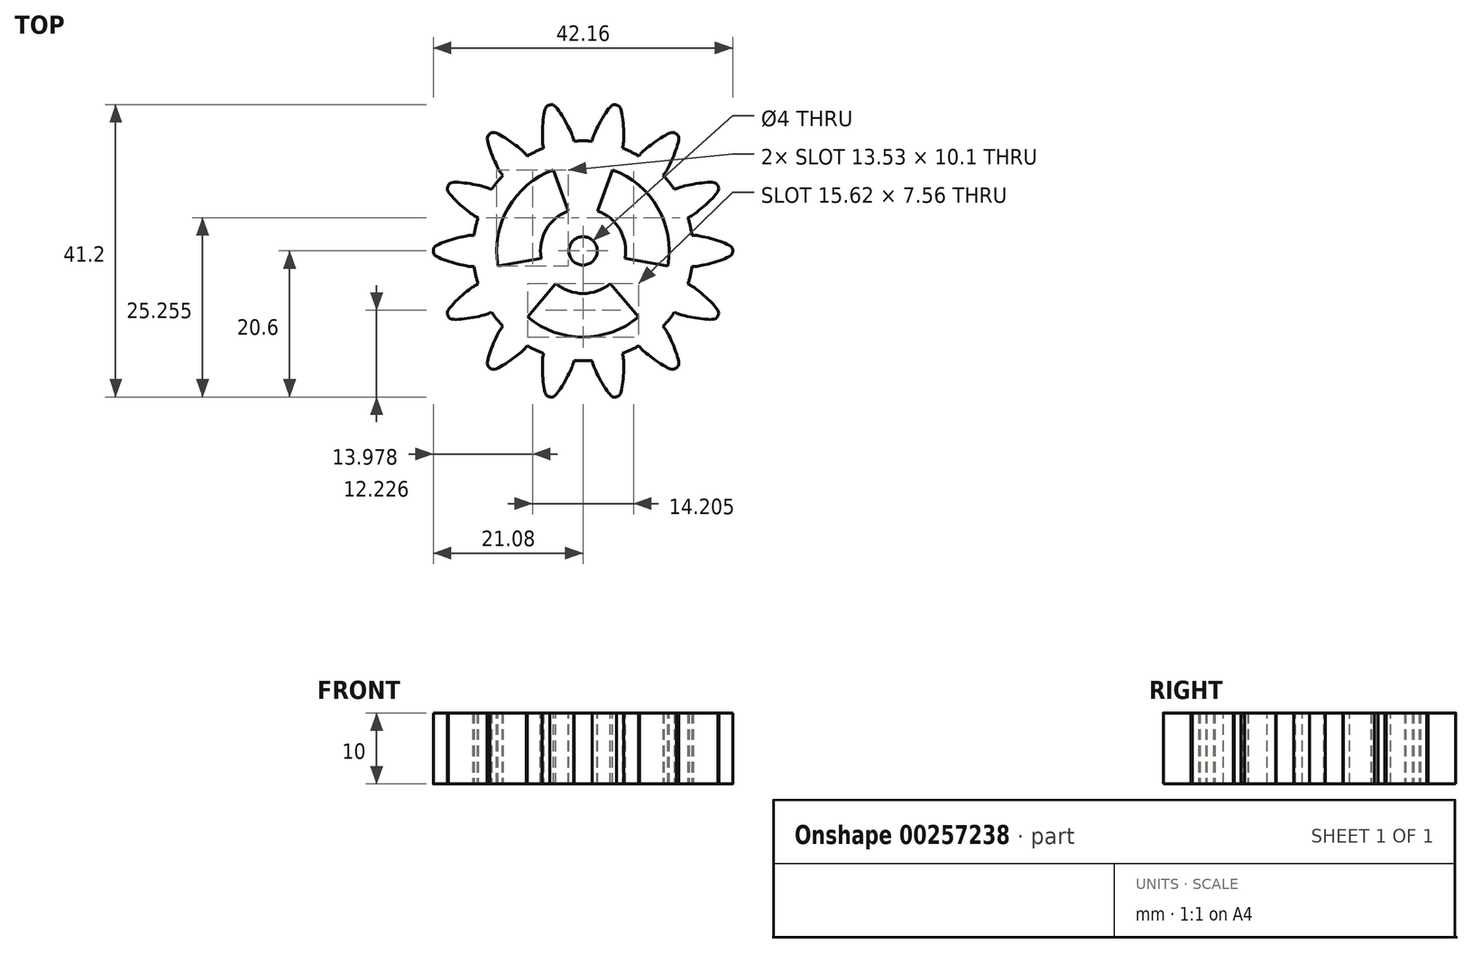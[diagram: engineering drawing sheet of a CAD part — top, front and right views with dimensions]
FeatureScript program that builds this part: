
annotation { "Feature Type Name" : "Feature", "Feature Type Description" : "" }
export const myFeature = defineFeature(function(context is Context, id is Id, definition is map)
    precondition{}
    {
        {
            var Q0;
            Q0=qCreatedBy(makeId("Top.planeOp"),FACE);
            var sketch = newSketch(context, id + "F0", { "sketchPlane" : qUnion([Q0])});
            skLineSegment(sketch, "E0.bottom", {"start": v(-13.86, -2.2) * mm, "end": v(-15.52, -2.2) * mm});
            skLineSegment(sketch, "E0.top", {"start": v(-13.86, 2.2) * mm, "end": v(-15.52, 2.2) * mm});
            skLineSegment(sketch, "E0.left", {"start": v(-13.86, -2.2) * mm, "end": v(-13.86, 2.2) * mm});
            skLineSegment(sketch, "E0.right", {"start": v(-15.52, -2.2) * mm, "end": v(-15.52, 2.2) * mm});
            skPoint(sketch, "E0.middle", {"position": v(-14.69, 0) * mm});
            skFitSpline(sketch, "E1", {"points": [v(-15.52, 2.2) * mm, v(-16.5, 2.1) * mm, v(-20.82, 0.63) * mm, v(-21.08, 0) * mm], "startDerivative": vector(-2.71, 0.04) * mm, "endDerivative": vector(0.07, -2.94) * mm});
            skLineSegment(sketch, "E2", {"start": v(-21.08, 0) * mm, "end": v(-15.52, 0) * mm});
            skFitSpline(sketch, "E3.MirrorCS", {"points": [v(-15.52, -2.2) * mm, v(-16.5, -2.1) * mm, v(-20.82, -0.63) * mm, v(-21.08, 0) * mm], "startDerivative": vector(-2.71, -0.04) * mm, "endDerivative": vector(0.07, 2.94) * mm});
            skCircle(sketch, "E4", {"center": v(0, 0) * mm, "radius": 5.34 * mm});
            skSolve(sketch);
        }
        {
            var Q0;
            Q0=makeQuery(id+"F0.imprint","IMPRINT",FACE,{"disambiguationData":[TD([[makeQuery(id+"F0.imprint","IMPRINT",EDGE,{"derivedFrom":sQuery(id+"F0.wireOp",EDGE,"E4")}),1.0]])]});
            extrude(context, id + "F1", {"entities" : qUnion([Q0]), "depth" : 10 * mm});
        }
        {
            var Q0;
            {var subQ0=sQuery(id+"F0.wireOp",EDGE,"E1");Q0=makeQuery(id+"F0.imprint","IMPRINT",FACE,{"disambiguationData":[TD([[makeQuery(id+"F0.imprint","IMPRINT",EDGE,{"derivedFrom":subQ0}),1.0]])]});}
            var Q1;
            {var subQ1=sQuery(id+"F0.wireOp",EDGE,"E0.bottom");Q1=makeQuery(id+"F0.imprint","IMPRINT",FACE,{"disambiguationData":[TD([[makeQuery(id+"F0.imprint","IMPRINT",EDGE,{"derivedFrom":subQ1}),-1.0]])]});}
            var Q2;
            {var subQ2=sQuery(id+"F0.wireOp",EDGE,"E2");Q2=makeQuery(id+"F0.imprint","IMPRINT",FACE,{"disambiguationData":[TD([[makeQuery(id+"F0.imprint","IMPRINT",EDGE,{"derivedFrom":subQ2}),-1.0]])]});}
            extrude(context, id + "F2", {"entities" : qUnion([Q0, Q1, Q2]), "depth" : 10 * mm});
        }
        {
            var Q0;
            Q0=makeQuery(id+"F2.opExtrude","SWEPT_BODY",BODY,{"disambiguationData":[OSD([sQuery(id+"F0.wireOp",EDGE,"E0.bottom"),sQuery(id+"F0.wireOp",EDGE,"E0.top"),sQuery(id+"F0.wireOp",EDGE,"E0.left"),sQuery(id+"F0.wireOp",EDGE,"E1"),sQuery(id+"F0.wireOp",EDGE,"E3.MirrorCS")])]});
            var Q1;
            Q1=makeQuery(id+"F1.opExtrude","CAP_EDGE",EDGE,{"disambiguationData":[OSD([sQuery(id+"F0.wireOp",EDGE,"E4")])],"isStart":false});
            circularPattern(context, id + "F3", {"entities" : qUnion([Q0]), "axis" : qUnion([Q1]), "angle" : 360 * degree, "instanceCount" : 14, "equalSpace" : true});
        }
        {
            var Q0;
            Q0=qCreatedBy(makeId("Top.planeOp"),FACE);
            var sketch = newSketch(context, id + "F4", { "sketchPlane" : qUnion([Q0])});
            skCircle(sketch, "E5", {"center": v(0, 0) * mm, "radius": 15.5 * mm});
            skSolve(sketch);
        }
        {
            var Q0;
            Q0=makeQuery(id+"F4.imprint","IMPRINT",FACE,{"disambiguationData":[TD([[makeQuery(id+"F4.imprint","IMPRINT",EDGE,{"derivedFrom":sQuery(id+"F4.wireOp",EDGE,"E5")}),1.0]])]});
            extrude(context, id + "F5", {"entities" : qUnion([Q0]), "operationType" : NewBodyOperationType.ADD, "depth" : 10 * mm});
        }
        {
            var Q0;
            {var subQ0=makeQuery(id+"F2.opExtrude","CAP_FACE",FACE,{"disambiguationData":[OSD([sQuery(id+"F0.wireOp",EDGE,"E0.bottom"),sQuery(id+"F0.wireOp",EDGE,"E0.top"),sQuery(id+"F0.wireOp",EDGE,"E0.left"),sQuery(id+"F0.wireOp",EDGE,"E1"),sQuery(id+"F0.wireOp",EDGE,"E3.MirrorCS")])],"isStart":false});Q0=makeQuery(id+"F5.boolean.opBoolean","MERGE",FACE,{"derivedFrom":[makeQuery(id+"F1.opExtrude","CAP_FACE",FACE,{"disambiguationData":[OSD([sQuery(id+"F0.wireOp",EDGE,"E4")])],"isStart":false}),subQ0,makeQuery(id+"F3.opPattern","COPY",FACE,{"derivedFrom":subQ0,"instanceName":"1"}),makeQuery(id+"F3.opPattern","COPY",FACE,{"derivedFrom":subQ0,"instanceName":"2"}),makeQuery(id+"F3.opPattern","COPY",FACE,{"derivedFrom":subQ0,"instanceName":"3"}),makeQuery(id+"F3.opPattern","COPY",FACE,{"derivedFrom":subQ0,"instanceName":"4"}),makeQuery(id+"F3.opPattern","COPY",FACE,{"derivedFrom":subQ0,"instanceName":"5"}),makeQuery(id+"F3.opPattern","COPY",FACE,{"derivedFrom":subQ0,"instanceName":"6"}),makeQuery(id+"F3.opPattern","COPY",FACE,{"derivedFrom":subQ0,"instanceName":"7"}),makeQuery(id+"F3.opPattern","COPY",FACE,{"derivedFrom":subQ0,"instanceName":"8"}),makeQuery(id+"F3.opPattern","COPY",FACE,{"derivedFrom":subQ0,"instanceName":"9"}),makeQuery(id+"F3.opPattern","COPY",FACE,{"derivedFrom":subQ0,"instanceName":"10"}),makeQuery(id+"F3.opPattern","COPY",FACE,{"derivedFrom":subQ0,"instanceName":"11"}),makeQuery(id+"F3.opPattern","COPY",FACE,{"derivedFrom":subQ0,"instanceName":"12"}),makeQuery(id+"F3.opPattern","COPY",FACE,{"derivedFrom":subQ0,"instanceName":"13"}),makeQuery(id+"F3.opPattern","COPY",FACE,{"derivedFrom":subQ0,"instanceName":"14"}),makeQuery(id+"F3.opPattern","COPY",FACE,{"derivedFrom":subQ0,"instanceName":"15"}),makeQuery(id+"F5.opExtrude","CAP_FACE",FACE,{"disambiguationData":[OSD([sQuery(id+"F4.wireOp",EDGE,"E5")])],"isStart":false})]});}
            var sketch = newSketch(context, id + "F6", { "sketchPlane" : qUnion([Q0])});
            skLineSegment(sketch, "E6", {"start": v(0, 0) * mm, "end": v(0, -15.09) * mm, "construction": true});
            skArc(sketch, "E7", {"start": v(-7.81, -9.3) * mm, "mid": v(0, -12.15) * mm, "end": v(7.81, -9.3) * mm});
            skArc(sketch, "E8", {"start": v(-3.86, -4.6) * mm, "mid": v(0, -6) * mm, "end": v(3.86, -4.6) * mm});
            skLineSegment(sketch, "E9", {"start": v(-3.86, -4.6) * mm, "end": v(-7.81, -9.3) * mm});
            skLineSegment(sketch, "E10", {"start": v(3.86, -4.6) * mm, "end": v(7.81, -9.3) * mm});
            skArc(sketch, "E11.1.0", {"start": v(5.9, -1.04) * mm, "mid": v(5.2, 3) * mm, "end": v(2.05, 5.64) * mm});
            skLineSegment(sketch, "E11.1.1", {"start": v(5.9, -1.04) * mm, "end": v(11.97, -2.11) * mm});
            skArc(sketch, "E11.1.2", {"start": v(11.97, -2.11) * mm, "mid": v(10.52, 6.08) * mm, "end": v(4.16, 11.42) * mm});
            skLineSegment(sketch, "E11.1.3", {"start": v(2.05, 5.64) * mm, "end": v(4.16, 11.42) * mm});
            skArc(sketch, "E11.2.0", {"start": v(-2.05, 5.64) * mm, "mid": v(-5.2, 3) * mm, "end": v(-5.9, -1.04) * mm});
            skLineSegment(sketch, "E11.2.1", {"start": v(-2.05, 5.64) * mm, "end": v(-4.16, 11.42) * mm});
            skArc(sketch, "E11.2.2", {"start": v(-4.16, 11.42) * mm, "mid": v(-10.52, 6.08) * mm, "end": v(-11.97, -2.11) * mm});
            skLineSegment(sketch, "E11.2.3", {"start": v(-5.9, -1.04) * mm, "end": v(-11.97, -2.11) * mm});
            skSolve(sketch);
        }
        {
            var Q0;
            {var subQ0=makeQuery(id+"F2.opExtrude","CAP_FACE",FACE,{"disambiguationData":[OSD([sQuery(id+"F0.wireOp",EDGE,"E0.bottom"),sQuery(id+"F0.wireOp",EDGE,"E0.top"),sQuery(id+"F0.wireOp",EDGE,"E0.left"),sQuery(id+"F0.wireOp",EDGE,"E1"),sQuery(id+"F0.wireOp",EDGE,"E3.MirrorCS")])],"isStart":false});Q0=makeQuery(id+"F5.boolean.opBoolean","MERGE",FACE,{"derivedFrom":[makeQuery(id+"F1.opExtrude","CAP_FACE",FACE,{"disambiguationData":[OSD([sQuery(id+"F0.wireOp",EDGE,"E4")])],"isStart":false}),subQ0,makeQuery(id+"F3.opPattern","COPY",FACE,{"derivedFrom":subQ0,"instanceName":"1"}),makeQuery(id+"F3.opPattern","COPY",FACE,{"derivedFrom":subQ0,"instanceName":"2"}),makeQuery(id+"F3.opPattern","COPY",FACE,{"derivedFrom":subQ0,"instanceName":"3"}),makeQuery(id+"F3.opPattern","COPY",FACE,{"derivedFrom":subQ0,"instanceName":"4"}),makeQuery(id+"F3.opPattern","COPY",FACE,{"derivedFrom":subQ0,"instanceName":"5"}),makeQuery(id+"F3.opPattern","COPY",FACE,{"derivedFrom":subQ0,"instanceName":"6"}),makeQuery(id+"F3.opPattern","COPY",FACE,{"derivedFrom":subQ0,"instanceName":"7"}),makeQuery(id+"F3.opPattern","COPY",FACE,{"derivedFrom":subQ0,"instanceName":"8"}),makeQuery(id+"F3.opPattern","COPY",FACE,{"derivedFrom":subQ0,"instanceName":"9"}),makeQuery(id+"F3.opPattern","COPY",FACE,{"derivedFrom":subQ0,"instanceName":"10"}),makeQuery(id+"F3.opPattern","COPY",FACE,{"derivedFrom":subQ0,"instanceName":"11"}),makeQuery(id+"F3.opPattern","COPY",FACE,{"derivedFrom":subQ0,"instanceName":"12"}),makeQuery(id+"F3.opPattern","COPY",FACE,{"derivedFrom":subQ0,"instanceName":"13"}),makeQuery(id+"F3.opPattern","COPY",FACE,{"derivedFrom":subQ0,"instanceName":"14"}),makeQuery(id+"F3.opPattern","COPY",FACE,{"derivedFrom":subQ0,"instanceName":"15"}),makeQuery(id+"F5.opExtrude","CAP_FACE",FACE,{"disambiguationData":[OSD([sQuery(id+"F4.wireOp",EDGE,"E5")])],"isStart":false})]});}
            var sketch = newSketch(context, id + "F7", { "sketchPlane" : qUnion([Q0])});
            skCircle(sketch, "E12", {"center": v(0, 0) * mm, "radius": 2 * mm});
            skSolve(sketch);
        }
        {
            var Q0;
            Q0=makeQuery(id+"F6.imprint","IMPRINT",FACE,{"disambiguationData":[TD([[makeQuery(id+"F6.imprint","IMPRINT",EDGE,{"derivedFrom":sQuery(id+"F6.wireOp",EDGE,"E11.2.0")}),-1.0]])]});
            var Q1;
            Q1=makeQuery(id+"F6.imprint","IMPRINT",FACE,{"disambiguationData":[TD([[makeQuery(id+"F6.imprint","IMPRINT",EDGE,{"derivedFrom":sQuery(id+"F6.wireOp",EDGE,"E7")}),1.0]])]});
            var Q2;
            Q2=makeQuery(id+"F6.imprint","IMPRINT",FACE,{"disambiguationData":[TD([[makeQuery(id+"F6.imprint","IMPRINT",EDGE,{"derivedFrom":sQuery(id+"F6.wireOp",EDGE,"E11.1.0")}),-1.0]])]});
            extrude(context, id + "F8", {"entities" : qUnion([Q0, Q1, Q2]), "operationType" : NewBodyOperationType.REMOVE, "endBound" : BoundingType.UP_TO_NEXT, "oppositeDirection" : true, "depth" : 25 * mm});
        }
        {
            var Q0;
            Q0=makeQuery(id+"F7.imprint","IMPRINT",FACE,{"disambiguationData":[TD([[makeQuery(id+"F7.imprint","IMPRINT",EDGE,{"derivedFrom":sQuery(id+"F7.wireOp",EDGE,"19837084-fc13-44eb-957a-b324fd168628.1.0.0")}),1.0]])]});
            var Q1;
            Q1=makeQuery(id+"F7.imprint","IMPRINT",FACE,{"disambiguationData":[TD([[makeQuery(id+"F7.imprint","IMPRINT",EDGE,{"derivedFrom":sQuery(id+"F7.wireOp",EDGE,"E12")}),1.0]])]});
            extrude(context, id + "F9", {"entities" : qUnion([Q0, Q1]), "operationType" : NewBodyOperationType.REMOVE, "endBound" : BoundingType.UP_TO_NEXT, "oppositeDirection" : true, "depth" : 25 * mm});
        }
    });
